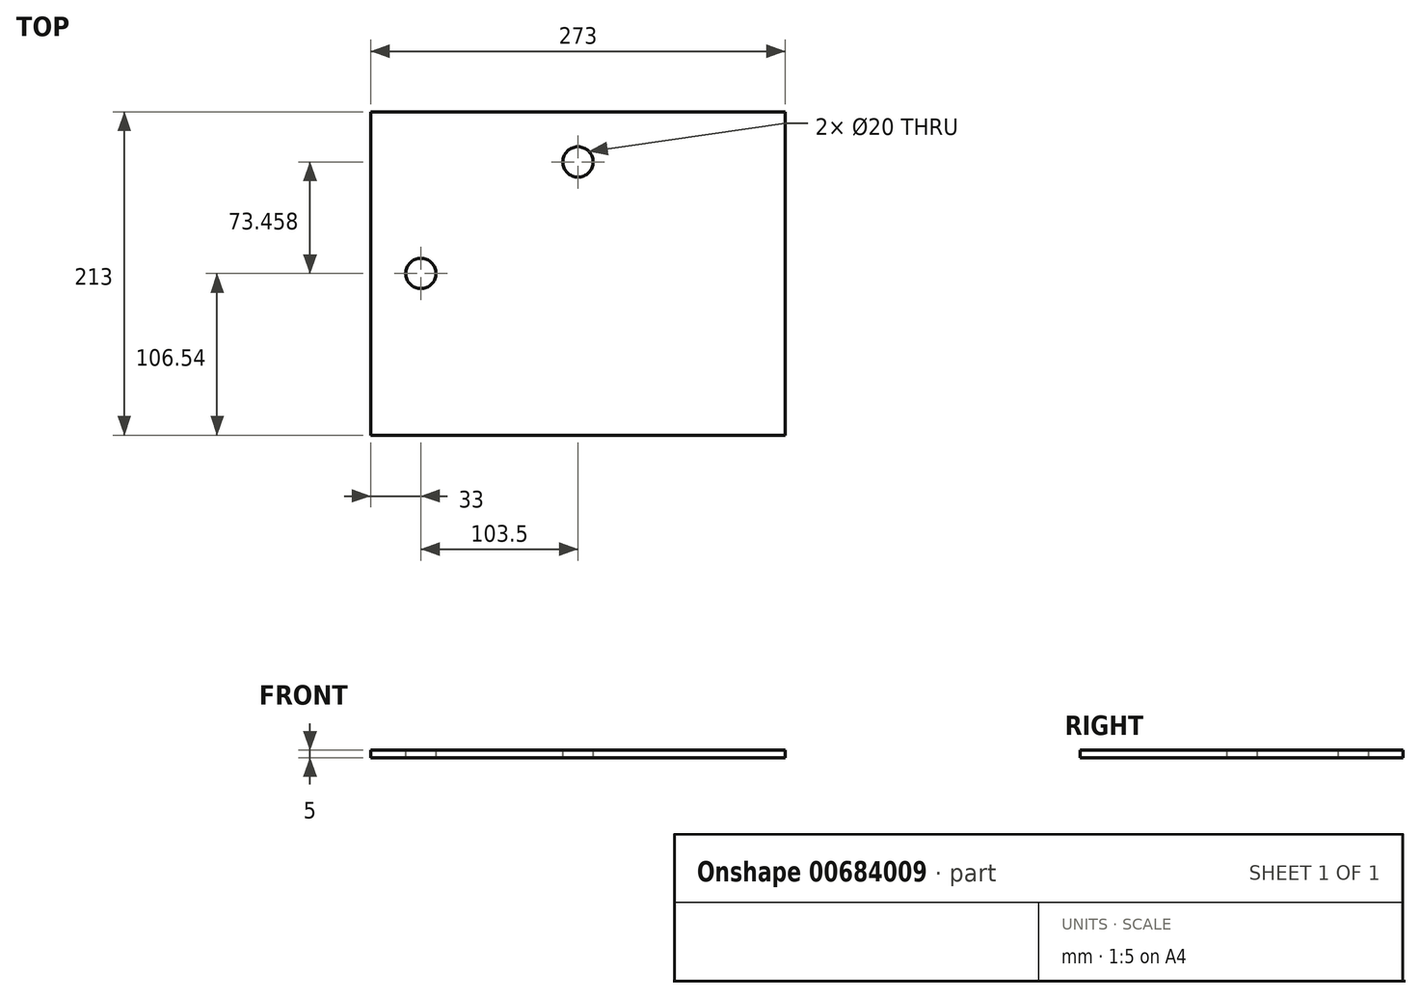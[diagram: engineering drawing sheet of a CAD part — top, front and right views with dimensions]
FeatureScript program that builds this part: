
annotation { "Feature Type Name" : "Feature", "Feature Type Description" : "" }
export const myFeature = defineFeature(function(context is Context, id is Id, definition is map)
    precondition{}
    {
        {
            var Q0;
            Q0=qCreatedBy(makeId("Top.planeOp"),FACE);
            var sketch = newSketch(context, id + "F0", { "sketchPlane" : qUnion([Q0])});
            skLineSegment(sketch, "E0.bottom", {"start": v(-136.5, 106.46) * mm, "end": v(136.5, 106.46) * mm});
            skLineSegment(sketch, "E0.top", {"start": v(-136.5, -106.54) * mm, "end": v(136.5, -106.54) * mm});
            skLineSegment(sketch, "E0.left", {"start": v(-136.5, 106.46) * mm, "end": v(-136.5, -106.54) * mm});
            skLineSegment(sketch, "E0.right", {"start": v(136.5, 106.46) * mm, "end": v(136.5, -106.54) * mm});
            skCircle(sketch, "E1", {"center": v(-103.5, 0) * mm, "radius": 10 * mm});
            skCircle(sketch, "E2", {"center": v(0, 73.46) * mm, "radius": 10 * mm});
            skLineSegment(sketch, "E3", {"start": v(0, 106.46) * mm, "end": v(0, -106.54) * mm, "construction": true});
            skLineSegment(sketch, "E4", {"start": v(0, -106.54) * mm, "end": v(136.5, -0.04) * mm, "construction": true});
            skLineSegment(sketch, "E5", {"start": v(136.5, -0.04) * mm, "end": v(-136.5, -0.04) * mm, "construction": true});
            skSolve(sketch);
        }
        {
            var Q0;
            Q0=makeQuery(id+"F0.imprint","IMPRINT",FACE,{"disambiguationData":[TD([[makeQuery(id+"F0.imprint","IMPRINT",EDGE,{"derivedFrom":sQuery(id+"F0.wireOp",EDGE,"E0.bottom")}),-1.0]])]});
            extrude(context, id + "F1", {"entities" : qUnion([Q0]), "depth" : 5 * mm, "offsetDistance" : 25 * mm});
        }
    });
